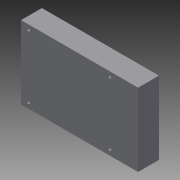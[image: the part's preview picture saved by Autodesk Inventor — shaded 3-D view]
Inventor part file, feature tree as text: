
AUTODESK INVENTOR PART (.ipt)
format: ipt  version: 2015 (Build 190159000, 159)  size: 85,504 bytes
history: native  units: mm
features: extrude x1, sketch x1
ambient origin geometry x8: Origin, YZ Plane, XZ Plane, XY Plane, X Axis, Y Axis, Z Axis, Center Point
bodies: Solid1 (feature_tree)
feature tree (2):
  extrude  "Extrusion1"  Depth=63.0mm
  sketch  "Sketch1"  dims[d0=101.0mm d2=63.0mm d3=3.0mm d4=3.0mm d5=3.0mm d6=3.0mm d9=3.9mm d10=3.9mm d11=6.1mm d12=70.2mm d14=6.1mm d15=70.2mm d16=18.0mm d17=0.0mm d18=54.2mm d19=54.2mm]
